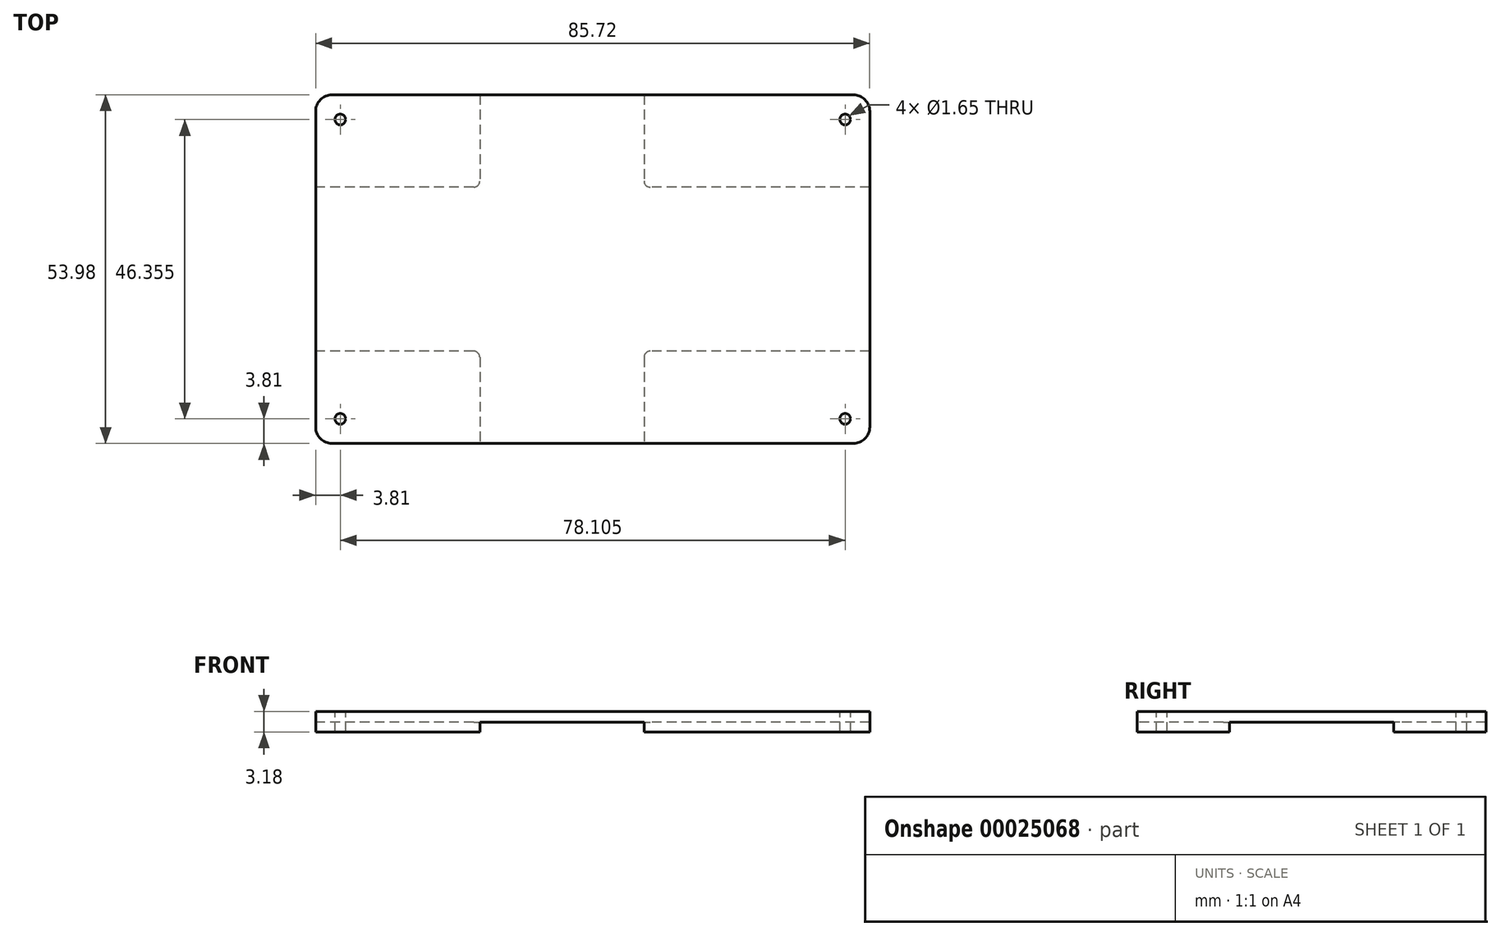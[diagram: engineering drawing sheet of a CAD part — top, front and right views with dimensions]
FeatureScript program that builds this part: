
annotation { "Feature Type Name" : "Feature", "Feature Type Description" : "" }
export const myFeature = defineFeature(function(context is Context, id is Id, definition is map)
    precondition{}
    {
        {
            var Q0;
            Q0=qCreatedBy(makeId("Top.planeOp"),FACE);
            var sketch = newSketch(context, id + "F0", { "sketchPlane" : qUnion([Q0])});
            skLineSegment(sketch, "E0.bottom", {"start": v(2.54, 0) * mm, "end": v(83.19, 0) * mm});
            skLineSegment(sketch, "E0.top", {"start": v(2.54, 53.97) * mm, "end": v(83.19, 53.97) * mm});
            skLineSegment(sketch, "E0.left", {"start": v(0, 2.54) * mm, "end": v(0, 51.43) * mm});
            skLineSegment(sketch, "E0.right", {"start": v(85.73, 2.54) * mm, "end": v(85.73, 51.44) * mm});
            skPoint(sketch, "E1.visualSharp", {"position": v(85.72, 53.97) * mm});
            skArc(sketch, "E1.filletArc", {"start": v(85.73, 51.44) * mm, "mid": v(84.98, 53.23) * mm, "end": v(83.19, 53.98) * mm});
            skPoint(sketch, "E2.visualSharp", {"position": v(85.73, 0) * mm});
            skArc(sketch, "E2.filletArc", {"start": v(83.19, 0) * mm, "mid": v(84.98, 0.74) * mm, "end": v(85.73, 2.54) * mm});
            skPoint(sketch, "E3.visualSharp", {"position": v(0, 0) * mm});
            skPoint(sketch, "E4.visualSharp", {"position": v(0, 53.97) * mm});
            skArc(sketch, "E4.filletArc", {"start": v(2.54, 53.97) * mm, "mid": v(0.74, 53.23) * mm, "end": v(0, 51.43) * mm});
            skArc(sketch, "E5.filletArc", {"start": v(0, 2.54) * mm, "mid": v(0.74, 0.74) * mm, "end": v(2.54, 0) * mm});
            skSolve(sketch);
        }
        {
            var Q0;
            Q0=makeQuery(id+"F0.imprint","IMPRINT",FACE,{"disambiguationData":[TD([[makeQuery(id+"F0.imprint","IMPRINT",EDGE,{"derivedFrom":sQuery(id+"F0.wireOp",EDGE,"E0.bottom")}),1.0]])]});
            extrude(context, id + "F1", {"entities" : qUnion([Q0]), "depth" : 3.17 * mm});
        }
        {
            var Q0;
            Q0=makeQuery(id+"F1.opExtrude","CAP_FACE",FACE,{"disambiguationData":[OSD([sQuery(id+"F0.wireOp",EDGE,"E0.bottom"),sQuery(id+"F0.wireOp",EDGE,"E0.top"),sQuery(id+"F0.wireOp",EDGE,"E0.left"),sQuery(id+"F0.wireOp",EDGE,"E0.right"),sQuery(id+"F0.wireOp",EDGE,"E1.filletArc"),sQuery(id+"F0.wireOp",EDGE,"E2.filletArc"),sQuery(id+"F0.wireOp",EDGE,"E3.filletArc"),sQuery(id+"F0.wireOp",EDGE,"E4.filletArc")])],"isStart":false});
            var sketch = newSketch(context, id + "F2", { "sketchPlane" : qUnion([Q0])});
            skCircle(sketch, "E6", {"center": v(3.8, 50.16) * mm, "radius": 0.83 * mm});
            skLineSegment(sketch, "E7.bottom", {"start": v(3.8, 50.16) * mm, "end": v(81.92, 50.16) * mm, "construction": true});
            skLineSegment(sketch, "E7.top", {"start": v(3.81, 3.8) * mm, "end": v(81.92, 3.81) * mm, "construction": true});
            skLineSegment(sketch, "E7.left", {"start": v(3.8, 50.16) * mm, "end": v(3.81, 3.8) * mm, "construction": true});
            skLineSegment(sketch, "E7.right", {"start": v(81.92, 50.16) * mm, "end": v(81.92, 3.81) * mm, "construction": true});
            skCircle(sketch, "E8", {"center": v(81.92, 50.16) * mm, "radius": 0.83 * mm});
            skCircle(sketch, "E9", {"center": v(81.92, 3.81) * mm, "radius": 0.83 * mm});
            skCircle(sketch, "E10", {"center": v(3.81, 3.8) * mm, "radius": 0.83 * mm});
            skSolve(sketch);
        }
        {
            var Q0;
            Q0 = qSketchRegion(id + "F2", true);
            extrude(context, id + "F3", {"entities" : qUnion([Q0]), "operationType" : NewBodyOperationType.REMOVE, "endBound" : BoundingType.THROUGH_ALL, "oppositeDirection" : true, "depth" : 25.4 * mm});
        }
        {
            var Q0;
            Q0=makeQuery(id+"F1.opExtrude","CAP_FACE",FACE,{"disambiguationData":[OSD([sQuery(id+"F0.wireOp",EDGE,"E0.bottom"),sQuery(id+"F0.wireOp",EDGE,"E0.top"),sQuery(id+"F0.wireOp",EDGE,"E0.left"),sQuery(id+"F0.wireOp",EDGE,"E0.right"),sQuery(id+"F0.wireOp",EDGE,"E1.filletArc"),sQuery(id+"F0.wireOp",EDGE,"E2.filletArc"),sQuery(id+"F0.wireOp",EDGE,"E3.filletArc"),sQuery(id+"F0.wireOp",EDGE,"E4.filletArc")])],"isStart":true});
            var sketch = newSketch(context, id + "F4", { "sketchPlane" : qUnion([Q0])});
            skLineSegment(sketch, "E11.bottom", {"start": v(85.73, -39.69) * mm, "end": v(50.8, -39.69) * mm});
            skLineSegment(sketch, "E11.top", {"start": v(85.73, -14.29) * mm, "end": v(50.8, -14.29) * mm});
            skLineSegment(sketch, "E11.left", {"start": v(85.73, -39.69) * mm, "end": v(85.73, -14.29) * mm});
            skLineSegment(sketch, "E11.right", {"start": v(0, -39.69) * mm, "end": v(0, -14.29) * mm});
            skLineSegment(sketch, "E12.bottom", {"start": v(50.8, -53.97) * mm, "end": v(25.4, -53.97) * mm});
            skLineSegment(sketch, "E12.top", {"start": v(50.8, 0) * mm, "end": v(25.4, 0) * mm});
            skLineSegment(sketch, "E12.left", {"start": v(50.8, -53.97) * mm, "end": v(50.8, -39.69) * mm});
            skLineSegment(sketch, "E12.right", {"start": v(25.4, -53.97) * mm, "end": v(25.4, -39.69) * mm});
            skLineSegment(sketch, "E13.trimOffspring", {"start": v(25.4, -39.69) * mm, "end": v(0, -39.69) * mm});
            skLineSegment(sketch, "E14.trimOffspring", {"start": v(25.4, -14.29) * mm, "end": v(0, -14.29) * mm});
            skLineSegment(sketch, "E15.trimOffspring", {"start": v(50.8, -14.29) * mm, "end": v(50.8, 0) * mm});
            skLineSegment(sketch, "E16.trimOffspring", {"start": v(25.4, -14.29) * mm, "end": v(25.4, 0) * mm});
            skLineSegment(sketch, "E17", {"start": v(0, -26.99) * mm, "end": v(85.73, -26.99) * mm, "construction": true});
            skSolve(sketch);
        }
        {
            var Q0;
            Q0 = qSketchRegion(id + "F4", true);
            extrude(context, id + "F5", {"entities" : qUnion([Q0]), "operationType" : NewBodyOperationType.REMOVE, "oppositeDirection" : true, "depth" : 1.52 * mm});
        }
        {
            var Q0;
            Q0=makeQuery(id+"F5.boolean.opBoolean","COPY",EDGE,{"derivedFrom":makeQuery(id+"F5.opExtrude","SWEPT_EDGE",EDGE,{"disambiguationData":[OSD([sQuery(id+"F4.wireOp",EDGE,"E11.bottom"),sQuery(id+"F4.wireOp",EDGE,"E12.left")])]})});
            var Q1;
            Q1=makeQuery(id+"F5.boolean.opBoolean","COPY",EDGE,{"derivedFrom":makeQuery(id+"F5.opExtrude","SWEPT_EDGE",EDGE,{"disambiguationData":[OSD([sQuery(id+"F4.wireOp",EDGE,"E12.right"),sQuery(id+"F4.wireOp",EDGE,"E13.trimOffspring")])]})});
            var Q2;
            Q2=makeQuery(id+"F5.boolean.opBoolean","COPY",EDGE,{"derivedFrom":makeQuery(id+"F5.opExtrude","SWEPT_EDGE",EDGE,{"disambiguationData":[OSD([sQuery(id+"F4.wireOp",EDGE,"E11.top"),sQuery(id+"F4.wireOp",EDGE,"E15.trimOffspring")])]})});
            var Q3;
            Q3=makeQuery(id+"F5.boolean.opBoolean","COPY",EDGE,{"derivedFrom":makeQuery(id+"F5.opExtrude","SWEPT_EDGE",EDGE,{"disambiguationData":[OSD([sQuery(id+"F4.wireOp",EDGE,"E14.trimOffspring"),sQuery(id+"F4.wireOp",EDGE,"E16.trimOffspring")])]})});
            var Q4;
            Q4=makeQuery(id+"F5.boolean.opBoolean","COPY",EDGE,{"derivedFrom":makeQuery(id+"F5.opExtrude","SWEPT_EDGE",EDGE,{"disambiguationData":[OSD([sQuery(id+"F0.wireOp",EDGE,"E0.right"),sQuery(id+"F4.wireOp",EDGE,"E11.top"),sQuery(id+"F4.wireOp",EDGE,"E11.left")])]})});
            var Q5;
            Q5=makeQuery(id+"F5.boolean.opBoolean","COPY",EDGE,{"derivedFrom":makeQuery(id+"F5.opExtrude","SWEPT_EDGE",EDGE,{"disambiguationData":[OSD([sQuery(id+"F0.wireOp",EDGE,"E0.right"),sQuery(id+"F4.wireOp",EDGE,"E11.bottom"),sQuery(id+"F4.wireOp",EDGE,"E11.left")])]})});
            var Q6;
            Q6=makeQuery(id+"F5.boolean.opBoolean","COPY",EDGE,{"derivedFrom":makeQuery(id+"F5.opExtrude","SWEPT_EDGE",EDGE,{"disambiguationData":[OSD([sQuery(id+"F0.wireOp",EDGE,"E0.bottom"),sQuery(id+"F4.wireOp",EDGE,"E12.top"),sQuery(id+"F4.wireOp",EDGE,"E16.trimOffspring")])]})});
            var Q7;
            Q7=makeQuery(id+"F5.boolean.opBoolean","COPY",EDGE,{"derivedFrom":makeQuery(id+"F5.opExtrude","SWEPT_EDGE",EDGE,{"disambiguationData":[OSD([sQuery(id+"F0.wireOp",EDGE,"E0.left"),sQuery(id+"F4.wireOp",EDGE,"E11.right"),sQuery(id+"F4.wireOp",EDGE,"E14.trimOffspring")])]})});
            var Q8;
            Q8=makeQuery(id+"F5.boolean.opBoolean","COPY",EDGE,{"derivedFrom":makeQuery(id+"F5.opExtrude","SWEPT_EDGE",EDGE,{"disambiguationData":[OSD([sQuery(id+"F0.wireOp",EDGE,"E0.left"),sQuery(id+"F4.wireOp",EDGE,"E11.right"),sQuery(id+"F4.wireOp",EDGE,"E13.trimOffspring")])]})});
            var Q9;
            Q9=makeQuery(id+"F5.boolean.opBoolean","COPY",EDGE,{"derivedFrom":makeQuery(id+"F5.opExtrude","SWEPT_EDGE",EDGE,{"disambiguationData":[OSD([sQuery(id+"F0.wireOp",EDGE,"E0.top"),sQuery(id+"F4.wireOp",EDGE,"E12.bottom"),sQuery(id+"F4.wireOp",EDGE,"E12.right")])]})});
            var Q10;
            Q10=makeQuery(id+"F5.boolean.opBoolean","COPY",EDGE,{"derivedFrom":makeQuery(id+"F5.opExtrude","SWEPT_EDGE",EDGE,{"disambiguationData":[OSD([sQuery(id+"F0.wireOp",EDGE,"E0.top"),sQuery(id+"F4.wireOp",EDGE,"E12.bottom"),sQuery(id+"F4.wireOp",EDGE,"E12.left")])]})});
            var Q11;
            Q11=makeQuery(id+"F5.boolean.opBoolean","COPY",EDGE,{"derivedFrom":makeQuery(id+"F5.opExtrude","SWEPT_EDGE",EDGE,{"disambiguationData":[OSD([sQuery(id+"F0.wireOp",EDGE,"E0.bottom"),sQuery(id+"F4.wireOp",EDGE,"E12.top"),sQuery(id+"F4.wireOp",EDGE,"E15.trimOffspring")])]})});
            fillet(context, id + "F6", {"entities" : qUnion([Q0, Q1, Q2, Q3, Q4, Q5, Q6, Q7, Q8, Q9, Q10, Q11]), "radius" : 0.95 * mm, "tangentPropagation" : true, "allowEdgeOverflow" : false});
        }
    });
